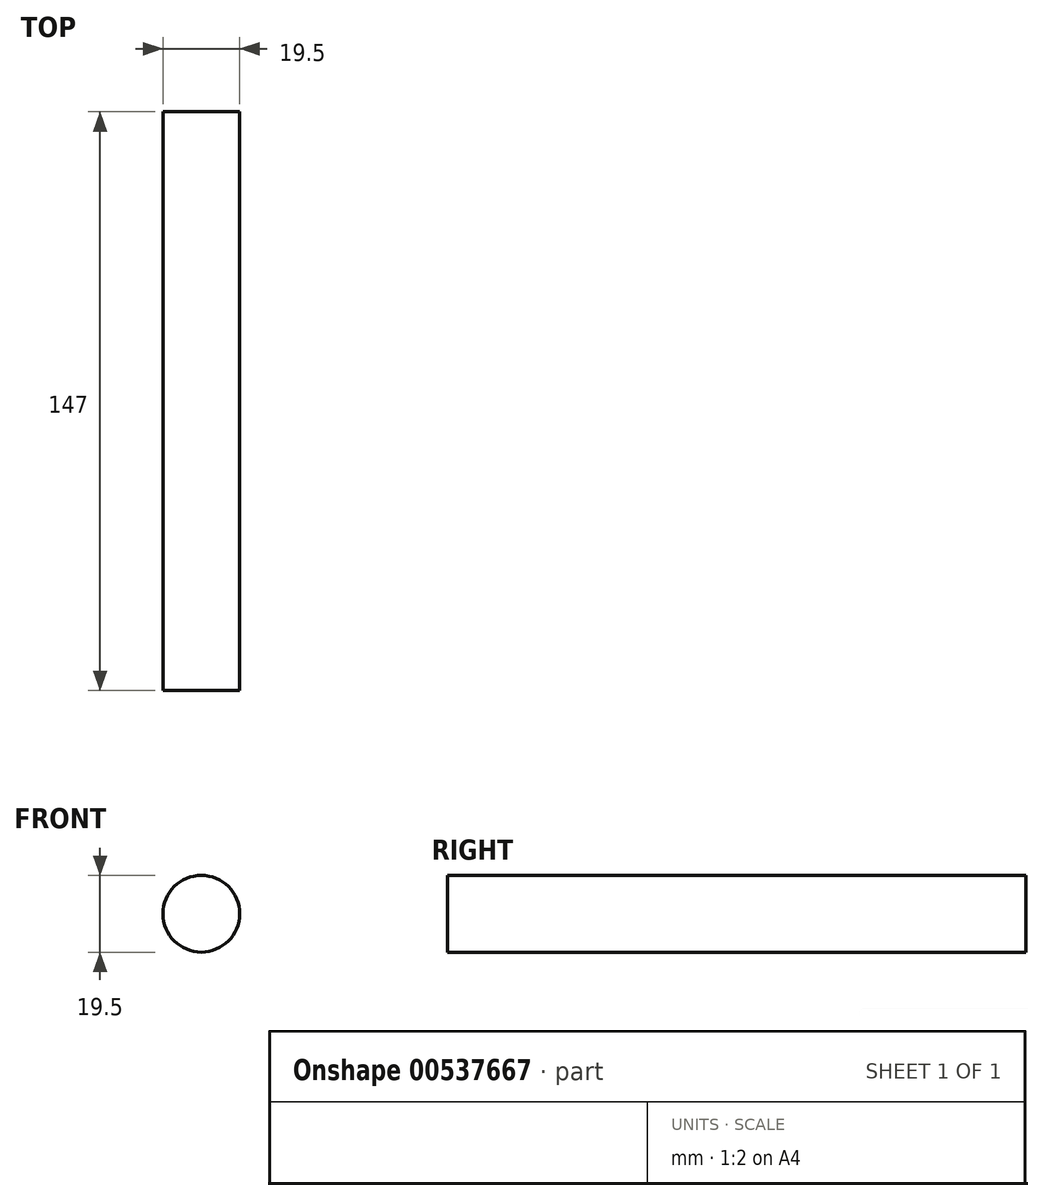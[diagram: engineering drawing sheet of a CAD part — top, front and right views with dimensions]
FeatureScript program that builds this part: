
annotation { "Feature Type Name" : "Feature", "Feature Type Description" : "" }
export const myFeature = defineFeature(function(context is Context, id is Id, definition is map)
    precondition{}
    {
        {
            var Q0;
            Q0=qCreatedBy(makeId("Front.planeOp"),FACE);
            var sketch = newSketch(context, id + "F0", { "sketchPlane" : qUnion([Q0])});
            skCircle(sketch, "E0", {"center": v(0, 0) * mm, "radius": 9.75 * mm});
            skSolve(sketch);
        }
        {
            var Q0;
            Q0=makeQuery(id+"F0.imprint","IMPRINT",FACE,{"disambiguationData":[TD([[makeQuery(id+"F0.imprint","IMPRINT",EDGE,{"derivedFrom":sQuery(id+"F0.wireOp",EDGE,"E0")}),1.0]])]});
            var Q1;
            Q1=sQuery(id+"F0.wireOp",EDGE,"E0");
            extrude(context, id + "F1", {"entities" : qUnion([Q0]), "surfaceEntities" : qUnion([Q1]), "oppositeDirection" : true, "depth" : 147 * mm, "offsetDistance" : 25 * mm});
        }
    });
